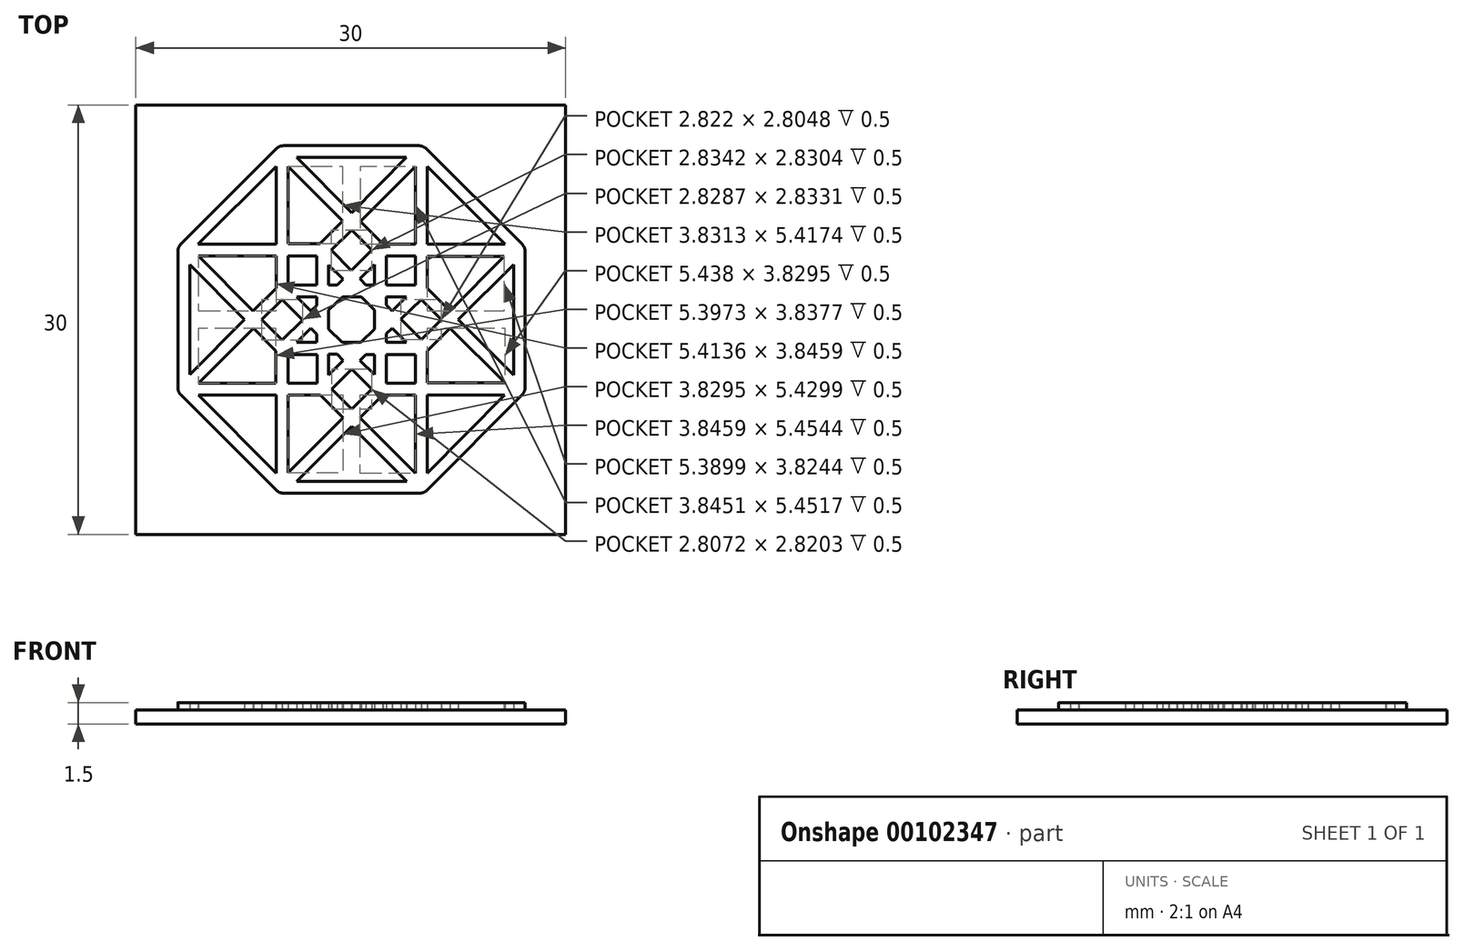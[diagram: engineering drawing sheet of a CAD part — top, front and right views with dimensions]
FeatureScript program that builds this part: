
annotation { "Feature Type Name" : "Feature", "Feature Type Description" : "" }
export const myFeature = defineFeature(function(context is Context, id is Id, definition is map)
    precondition{}
    {
        {
            var Q0;
            Q0=qCreatedBy(makeId("Top.planeOp"),FACE);
            var sketch = newSketch(context, id + "F0", { "sketchPlane" : qUnion([Q0])});
            skLineSegment(sketch, "E0.bottom", {"start": v(-41.44, 26.43) * mm, "end": v(-11.44, 26.43) * mm});
            skLineSegment(sketch, "E0.top", {"start": v(-41.44, -3.57) * mm, "end": v(-11.44, -3.57) * mm});
            skLineSegment(sketch, "E0.left", {"start": v(-41.44, 26.43) * mm, "end": v(-41.44, -3.57) * mm});
            skLineSegment(sketch, "E0.right", {"start": v(-11.44, 26.43) * mm, "end": v(-11.44, -3.57) * mm});
            skSolve(sketch);
        }
        {
            var Q0;
            Q0=makeQuery(id+"F0.imprint","IMPRINT",FACE,{"disambiguationData":[TD([[makeQuery(id+"F0.imprint","IMPRINT",EDGE,{"derivedFrom":sQuery(id+"F0.wireOp",EDGE,"E0.bottom")}),-1.0]])]});
            extrude(context, id + "F1", {"entities" : qUnion([Q0]), "oppositeDirection" : true, "depth" : 1 * mm});
        }
        {
            var Q0;
            Q0=makeQuery(id+"F1.opExtrude","CAP_FACE",FACE,{"disambiguationData":[OSD([sQuery(id+"F0.wireOp",EDGE,"E0.bottom"),sQuery(id+"F0.wireOp",EDGE,"E0.top"),sQuery(id+"F0.wireOp",EDGE,"E0.left"),sQuery(id+"F0.wireOp",EDGE,"E0.right")])],"isStart":true});
            var sketch = newSketch(context, id + "F2", { "sketchPlane" : qUnion([Q0])});
            skLineSegment(sketch, "E1", {"start": v(-27.98, 10.78) * mm, "end": v(-27.04, 9.85) * mm});
            skLineSegment(sketch, "E2", {"start": v(-27.04, 9.85) * mm, "end": v(-25.74, 9.85) * mm});
            skLineSegment(sketch, "E3", {"start": v(-25.74, 9.85) * mm, "end": v(-24.79, 10.77) * mm});
            skLineSegment(sketch, "E4", {"start": v(-24.79, 10.77) * mm, "end": v(-24.79, 12.1) * mm});
            skLineSegment(sketch, "E5", {"start": v(-24.79, 12.1) * mm, "end": v(-25.7, 13.04) * mm});
            skLineSegment(sketch, "E6", {"start": v(-25.7, 13.04) * mm, "end": v(-27.01, 13.04) * mm});
            skLineSegment(sketch, "E7", {"start": v(-27.01, 13.04) * mm, "end": v(-27.97, 12.1) * mm});
            skLineSegment(sketch, "E8", {"start": v(-27.97, 12.1) * mm, "end": v(-27.98, 10.78) * mm});
            skLineSegment(sketch, "E9", {"start": v(-23.95, 12.44) * mm, "end": v(-23.95, 13.04) * mm});
            skLineSegment(sketch, "E10", {"start": v(-23.95, 13.04) * mm, "end": v(-22.55, 13.04) * mm});
            skLineSegment(sketch, "E11", {"start": v(-22.55, 13.04) * mm, "end": v(-23.53, 12.03) * mm});
            skLineSegment(sketch, "E12", {"start": v(-23.53, 12.03) * mm, "end": v(-23.95, 12.44) * mm});
            skLineSegment(sketch, "E13", {"start": v(-23.96, 10.44) * mm, "end": v(-23.96, 9.84) * mm});
            skLineSegment(sketch, "E14", {"start": v(-23.96, 9.84) * mm, "end": v(-22.55, 9.84) * mm});
            skLineSegment(sketch, "E15", {"start": v(-22.55, 9.84) * mm, "end": v(-23.53, 10.85) * mm});
            skLineSegment(sketch, "E16", {"start": v(-23.53, 10.85) * mm, "end": v(-23.96, 10.44) * mm});
            skLineSegment(sketch, "E17", {"start": v(-22.94, 11.46) * mm, "end": v(-21.52, 10.03) * mm});
            skLineSegment(sketch, "E18", {"start": v(-21.52, 10.03) * mm, "end": v(-20.12, 11.42) * mm});
            skLineSegment(sketch, "E19", {"start": v(-20.12, 11.42) * mm, "end": v(-21.52, 12.83) * mm});
            skLineSegment(sketch, "E20", {"start": v(-21.52, 12.83) * mm, "end": v(-22.94, 11.46) * mm});
            skLineSegment(sketch, "E21", {"start": v(-27.97, 13.86) * mm, "end": v(-27.38, 13.86) * mm});
            skLineSegment(sketch, "E22", {"start": v(-27.38, 13.86) * mm, "end": v(-26.97, 14.28) * mm});
            skLineSegment(sketch, "E23", {"start": v(-26.97, 14.28) * mm, "end": v(-27.98, 15.26) * mm});
            skLineSegment(sketch, "E24", {"start": v(-27.98, 15.26) * mm, "end": v(-27.97, 13.86) * mm});
            skLineSegment(sketch, "E25", {"start": v(-25.37, 13.86) * mm, "end": v(-24.78, 13.86) * mm});
            skLineSegment(sketch, "E26", {"start": v(-24.78, 13.86) * mm, "end": v(-24.78, 15.28) * mm});
            skLineSegment(sketch, "E27", {"start": v(-24.78, 15.28) * mm, "end": v(-25.78, 14.28) * mm});
            skLineSegment(sketch, "E28", {"start": v(-25.78, 14.28) * mm, "end": v(-25.37, 13.86) * mm});
            skLineSegment(sketch, "E29", {"start": v(-27.8, 16.3) * mm, "end": v(-26.38, 14.88) * mm});
            skLineSegment(sketch, "E30", {"start": v(-26.38, 14.88) * mm, "end": v(-24.97, 16.29) * mm});
            skLineSegment(sketch, "E31", {"start": v(-24.97, 16.29) * mm, "end": v(-26.38, 17.7) * mm});
            skLineSegment(sketch, "E32", {"start": v(-26.38, 17.7) * mm, "end": v(-27.8, 16.3) * mm});
            skLineSegment(sketch, "E33", {"start": v(-30.22, 9.84) * mm, "end": v(-28.8, 9.84) * mm});
            skLineSegment(sketch, "E34", {"start": v(-28.8, 9.84) * mm, "end": v(-28.8, 10.43) * mm});
            skLineSegment(sketch, "E35", {"start": v(-28.8, 10.43) * mm, "end": v(-29.21, 10.83) * mm});
            skLineSegment(sketch, "E36", {"start": v(-29.21, 10.83) * mm, "end": v(-30.22, 9.84) * mm});
            skLineSegment(sketch, "E37", {"start": v(-30.2, 13.02) * mm, "end": v(-28.82, 13.02) * mm});
            skLineSegment(sketch, "E38", {"start": v(-28.82, 13.02) * mm, "end": v(-28.82, 12.43) * mm});
            skLineSegment(sketch, "E39", {"start": v(-28.82, 12.43) * mm, "end": v(-29.2, 12.04) * mm});
            skLineSegment(sketch, "E40", {"start": v(-29.2, 12.04) * mm, "end": v(-30.2, 13.02) * mm});
            skLineSegment(sketch, "E41", {"start": v(-32.64, 11.44) * mm, "end": v(-31.23, 10.02) * mm});
            skLineSegment(sketch, "E42", {"start": v(-31.23, 10.02) * mm, "end": v(-29.8, 11.42) * mm});
            skLineSegment(sketch, "E43", {"start": v(-29.8, 11.42) * mm, "end": v(-31.22, 12.85) * mm});
            skLineSegment(sketch, "E44", {"start": v(-31.22, 12.85) * mm, "end": v(-32.64, 11.44) * mm});
            skLineSegment(sketch, "E45", {"start": v(-27.98, 7.58) * mm, "end": v(-27.98, 9.01) * mm});
            skLineSegment(sketch, "E46", {"start": v(-27.98, 9.01) * mm, "end": v(-27.38, 9.01) * mm});
            skLineSegment(sketch, "E47", {"start": v(-27.38, 9.01) * mm, "end": v(-26.98, 8.58) * mm});
            skLineSegment(sketch, "E48", {"start": v(-26.98, 8.58) * mm, "end": v(-27.98, 7.58) * mm});
            skLineSegment(sketch, "E49", {"start": v(-25.37, 9) * mm, "end": v(-24.8, 9) * mm});
            skLineSegment(sketch, "E50", {"start": v(-24.8, 9) * mm, "end": v(-24.8, 7.59) * mm});
            skLineSegment(sketch, "E51", {"start": v(-24.8, 7.59) * mm, "end": v(-25.79, 8.58) * mm});
            skLineSegment(sketch, "E52", {"start": v(-25.79, 8.58) * mm, "end": v(-25.37, 9) * mm});
            skLineSegment(sketch, "E53", {"start": v(-26.37, 8) * mm, "end": v(-24.96, 6.57) * mm});
            skLineSegment(sketch, "E54", {"start": v(-24.96, 6.57) * mm, "end": v(-26.37, 5.17) * mm});
            skLineSegment(sketch, "E55", {"start": v(-26.37, 5.17) * mm, "end": v(-27.77, 6.58) * mm});
            skLineSegment(sketch, "E56", {"start": v(-27.77, 6.58) * mm, "end": v(-26.37, 8) * mm});
            skLineSegment(sketch, "E57.bottom", {"start": v(-30.81, 9) * mm, "end": v(-28.8, 9) * mm});
            skLineSegment(sketch, "E57.top", {"start": v(-30.81, 6.98) * mm, "end": v(-28.8, 6.98) * mm});
            skLineSegment(sketch, "E57.left", {"start": v(-30.81, 9) * mm, "end": v(-30.81, 6.98) * mm});
            skLineSegment(sketch, "E57.right", {"start": v(-28.8, 9) * mm, "end": v(-28.8, 6.98) * mm});
            skLineSegment(sketch, "E58.bottom", {"start": v(-23.95, 9) * mm, "end": v(-21.93, 9) * mm});
            skLineSegment(sketch, "E58.top", {"start": v(-23.95, 6.99) * mm, "end": v(-21.93, 6.99) * mm});
            skLineSegment(sketch, "E58.left", {"start": v(-23.95, 9) * mm, "end": v(-23.95, 6.99) * mm});
            skLineSegment(sketch, "E58.right", {"start": v(-21.93, 9) * mm, "end": v(-21.93, 6.99) * mm});
            skLineSegment(sketch, "E59.bottom", {"start": v(-30.82, 15.87) * mm, "end": v(-28.8, 15.87) * mm});
            skLineSegment(sketch, "E59.top", {"start": v(-30.82, 13.84) * mm, "end": v(-28.8, 13.84) * mm});
            skLineSegment(sketch, "E59.left", {"start": v(-30.82, 15.87) * mm, "end": v(-30.82, 13.84) * mm});
            skLineSegment(sketch, "E59.right", {"start": v(-28.8, 15.87) * mm, "end": v(-28.8, 13.84) * mm});
            skLineSegment(sketch, "E60.bottom", {"start": v(-23.95, 15.87) * mm, "end": v(-21.93, 15.87) * mm});
            skLineSegment(sketch, "E60.top", {"start": v(-23.95, 13.85) * mm, "end": v(-21.93, 13.85) * mm});
            skLineSegment(sketch, "E60.left", {"start": v(-23.95, 15.87) * mm, "end": v(-23.95, 13.85) * mm});
            skLineSegment(sketch, "E60.right", {"start": v(-21.93, 15.87) * mm, "end": v(-21.93, 13.85) * mm});
            skLineSegment(sketch, "E61", {"start": v(-37.09, 16.7) * mm, "end": v(-31.64, 16.7) * mm});
            skLineSegment(sketch, "E62", {"start": v(-31.64, 16.7) * mm, "end": v(-31.64, 22.15) * mm});
            skLineSegment(sketch, "E63", {"start": v(-31.64, 22.15) * mm, "end": v(-37.09, 16.7) * mm});
            skLineSegment(sketch, "E64", {"start": v(-30.82, 22.15) * mm, "end": v(-30.82, 16.73) * mm});
            skLineSegment(sketch, "E65", {"start": v(-30.82, 16.73) * mm, "end": v(-28.58, 16.73) * mm});
            skLineSegment(sketch, "E66", {"start": v(-28.58, 16.73) * mm, "end": v(-26.99, 18.31) * mm});
            skLineSegment(sketch, "E67", {"start": v(-26.99, 18.31) * mm, "end": v(-30.82, 22.15) * mm});
            skLineSegment(sketch, "E68", {"start": v(-30.21, 22.76) * mm, "end": v(-22.55, 22.76) * mm});
            skLineSegment(sketch, "E69", {"start": v(-22.55, 22.76) * mm, "end": v(-26.38, 18.9) * mm});
            skLineSegment(sketch, "E70", {"start": v(-26.38, 18.9) * mm, "end": v(-30.21, 22.76) * mm});
            skLineSegment(sketch, "E71", {"start": v(-21.93, 22.15) * mm, "end": v(-21.93, 16.7) * mm});
            skLineSegment(sketch, "E72", {"start": v(-21.93, 16.7) * mm, "end": v(-24.19, 16.7) * mm});
            skLineSegment(sketch, "E73", {"start": v(-24.19, 16.7) * mm, "end": v(-25.78, 18.3) * mm});
            skLineSegment(sketch, "E74", {"start": v(-25.78, 18.3) * mm, "end": v(-21.93, 22.15) * mm});
            skLineSegment(sketch, "E75", {"start": v(-21.1, 22.15) * mm, "end": v(-21.1, 16.71) * mm});
            skLineSegment(sketch, "E76", {"start": v(-21.1, 16.71) * mm, "end": v(-15.68, 16.71) * mm});
            skLineSegment(sketch, "E77", {"start": v(-15.68, 16.71) * mm, "end": v(-21.1, 22.15) * mm});
            skLineSegment(sketch, "E78", {"start": v(-21.1, 13.62) * mm, "end": v(-21.1, 15.86) * mm});
            skLineSegment(sketch, "E79", {"start": v(-21.1, 15.86) * mm, "end": v(-15.72, 15.86) * mm});
            skLineSegment(sketch, "E80", {"start": v(-15.72, 15.86) * mm, "end": v(-19.52, 12.04) * mm});
            skLineSegment(sketch, "E81", {"start": v(-19.52, 12.04) * mm, "end": v(-21.1, 13.62) * mm});
            skLineSegment(sketch, "E82", {"start": v(-15.07, 15.3) * mm, "end": v(-15.07, 7.57) * mm});
            skLineSegment(sketch, "E83", {"start": v(-15.07, 7.57) * mm, "end": v(-18.92, 11.44) * mm});
            skLineSegment(sketch, "E84", {"start": v(-18.92, 11.44) * mm, "end": v(-15.07, 15.3) * mm});
            skLineSegment(sketch, "E85", {"start": v(-21.1, 9.24) * mm, "end": v(-21.1, 7.02) * mm});
            skLineSegment(sketch, "E86", {"start": v(-21.1, 7.02) * mm, "end": v(-15.67, 7.02) * mm});
            skLineSegment(sketch, "E87", {"start": v(-15.67, 7.02) * mm, "end": v(-19.52, 10.84) * mm});
            skLineSegment(sketch, "E88", {"start": v(-19.52, 10.84) * mm, "end": v(-21.1, 9.24) * mm});
            skLineSegment(sketch, "E89", {"start": v(-21.1, 0.72) * mm, "end": v(-21.1, 6.16) * mm});
            skLineSegment(sketch, "E90", {"start": v(-21.1, 6.16) * mm, "end": v(-15.7, 6.16) * mm});
            skLineSegment(sketch, "E91", {"start": v(-15.7, 6.16) * mm, "end": v(-21.1, 0.72) * mm});
            skLineSegment(sketch, "E92", {"start": v(-24.2, 6.16) * mm, "end": v(-21.93, 6.16) * mm});
            skLineSegment(sketch, "E93", {"start": v(-21.93, 6.16) * mm, "end": v(-21.93, 0.7) * mm});
            skLineSegment(sketch, "E94", {"start": v(-21.93, 0.7) * mm, "end": v(-25.78, 4.57) * mm});
            skLineSegment(sketch, "E95", {"start": v(-25.78, 4.57) * mm, "end": v(-24.2, 6.16) * mm});
            skLineSegment(sketch, "E96", {"start": v(-30.21, 0.14) * mm, "end": v(-22.54, 0.14) * mm});
            skLineSegment(sketch, "E97", {"start": v(-22.54, 0.14) * mm, "end": v(-26.38, 3.97) * mm});
            skLineSegment(sketch, "E98", {"start": v(-26.38, 3.97) * mm, "end": v(-30.21, 0.14) * mm});
            skLineSegment(sketch, "E99", {"start": v(-30.8, 0.73) * mm, "end": v(-30.8, 6.16) * mm});
            skLineSegment(sketch, "E100", {"start": v(-30.8, 6.16) * mm, "end": v(-28.56, 6.16) * mm});
            skLineSegment(sketch, "E101", {"start": v(-28.56, 6.16) * mm, "end": v(-26.98, 4.57) * mm});
            skLineSegment(sketch, "E102", {"start": v(-26.98, 4.57) * mm, "end": v(-30.8, 0.73) * mm});
            skLineSegment(sketch, "E103", {"start": v(-31.65, 0.72) * mm, "end": v(-31.65, 6.16) * mm});
            skLineSegment(sketch, "E104", {"start": v(-31.65, 6.16) * mm, "end": v(-37.08, 6.16) * mm});
            skLineSegment(sketch, "E105", {"start": v(-37.08, 6.16) * mm, "end": v(-31.65, 0.72) * mm});
            skLineSegment(sketch, "E106", {"start": v(-37.06, 7) * mm, "end": v(-31.67, 7) * mm});
            skLineSegment(sketch, "E107", {"start": v(-31.67, 7) * mm, "end": v(-31.67, 9.24) * mm});
            skLineSegment(sketch, "E108", {"start": v(-31.67, 9.24) * mm, "end": v(-33.23, 10.84) * mm});
            skLineSegment(sketch, "E109", {"start": v(-33.23, 10.84) * mm, "end": v(-37.06, 7) * mm});
            skLineSegment(sketch, "E110", {"start": v(-37.67, 7.6) * mm, "end": v(-37.67, 15.29) * mm});
            skLineSegment(sketch, "E111", {"start": v(-37.67, 15.29) * mm, "end": v(-33.85, 11.44) * mm});
            skLineSegment(sketch, "E112", {"start": v(-33.85, 11.44) * mm, "end": v(-37.67, 7.6) * mm});
            skLineSegment(sketch, "E113", {"start": v(-37.06, 15.87) * mm, "end": v(-31.64, 15.87) * mm});
            skLineSegment(sketch, "E114", {"start": v(-31.64, 15.87) * mm, "end": v(-31.64, 13.62) * mm});
            skLineSegment(sketch, "E115", {"start": v(-31.64, 13.62) * mm, "end": v(-33.24, 12.03) * mm});
            skLineSegment(sketch, "E116", {"start": v(-37.06, 15.87) * mm, "end": v(-33.24, 12.03) * mm});
            skLineSegment(sketch, "E117", {"start": v(-38.5, 6.39) * mm, "end": v(-38.5, 16.5) * mm});
            skLineSegment(sketch, "E118", {"start": v(-31.42, -0.69) * mm, "end": v(-21.32, -0.69) * mm});
            skLineSegment(sketch, "E119", {"start": v(-14.26, 6.4) * mm, "end": v(-14.26, 16.5) * mm});
            skLineSegment(sketch, "E120", {"start": v(-21.38, 23.58) * mm, "end": v(-31.42, 23.58) * mm});
            skLineSegment(sketch, "E121", {"start": v(-38.5, 16.5) * mm, "end": v(-31.42, 23.58) * mm});
            skLineSegment(sketch, "E122", {"start": v(-21.38, 23.58) * mm, "end": v(-14.26, 16.5) * mm});
            skLineSegment(sketch, "E123", {"start": v(-21.32, -0.69) * mm, "end": v(-14.26, 6.4) * mm});
            skLineSegment(sketch, "E124", {"start": v(-38.5, 6.39) * mm, "end": v(-31.42, -0.69) * mm});
            skSolve(sketch);
        }
        {
            var Q0;
            Q0=qSketchRegion(id+"F2",true);
            extrude(context, id + "F3", {"entities" : qUnion([Q0]), "operationType" : NewBodyOperationType.ADD, "depth" : 0.5 * mm});
        }
        {
            var Q0;
            Q0=makeQuery(id+"F3.opExtrude","SWEPT_EDGE",EDGE,{"disambiguationData":[OSD([sQuery(id+"F2.wireOp",EDGE,"E119"),sQuery(id+"F2.wireOp",EDGE,"E122")])]});
            var Q1;
            Q1=makeQuery(id+"F3.opExtrude","SWEPT_EDGE",EDGE,{"disambiguationData":[OSD([sQuery(id+"F2.wireOp",EDGE,"E119"),sQuery(id+"F2.wireOp",EDGE,"E123")])]});
            var Q2;
            Q2=makeQuery(id+"F3.opExtrude","SWEPT_EDGE",EDGE,{"disambiguationData":[OSD([sQuery(id+"F2.wireOp",EDGE,"E118"),sQuery(id+"F2.wireOp",EDGE,"E123")])]});
            var Q3;
            Q3=makeQuery(id+"F3.opExtrude","SWEPT_EDGE",EDGE,{"disambiguationData":[OSD([sQuery(id+"F2.wireOp",EDGE,"E118"),sQuery(id+"F2.wireOp",EDGE,"E124")])]});
            var Q4;
            Q4=makeQuery(id+"F3.opExtrude","SWEPT_EDGE",EDGE,{"disambiguationData":[OSD([sQuery(id+"F2.wireOp",EDGE,"E117"),sQuery(id+"F2.wireOp",EDGE,"E124")])]});
            var Q5;
            Q5=makeQuery(id+"F3.opExtrude","SWEPT_EDGE",EDGE,{"disambiguationData":[OSD([sQuery(id+"F2.wireOp",EDGE,"E120"),sQuery(id+"F2.wireOp",EDGE,"E122")])]});
            var Q6;
            Q6=makeQuery(id+"F3.opExtrude","SWEPT_EDGE",EDGE,{"disambiguationData":[OSD([sQuery(id+"F2.wireOp",EDGE,"E120"),sQuery(id+"F2.wireOp",EDGE,"E121")])]});
            var Q7;
            Q7=makeQuery(id+"F3.opExtrude","SWEPT_EDGE",EDGE,{"disambiguationData":[OSD([sQuery(id+"F2.wireOp",EDGE,"E117"),sQuery(id+"F2.wireOp",EDGE,"E121")])]});
            fillet(context, id + "F4", {"entities" : qUnion([Q0, Q1, Q2, Q3, Q4, Q5, Q6, Q7]), "radius" : 0.7 * mm, "tangentPropagation" : true, "allowEdgeOverflow" : false});
        }
    });
